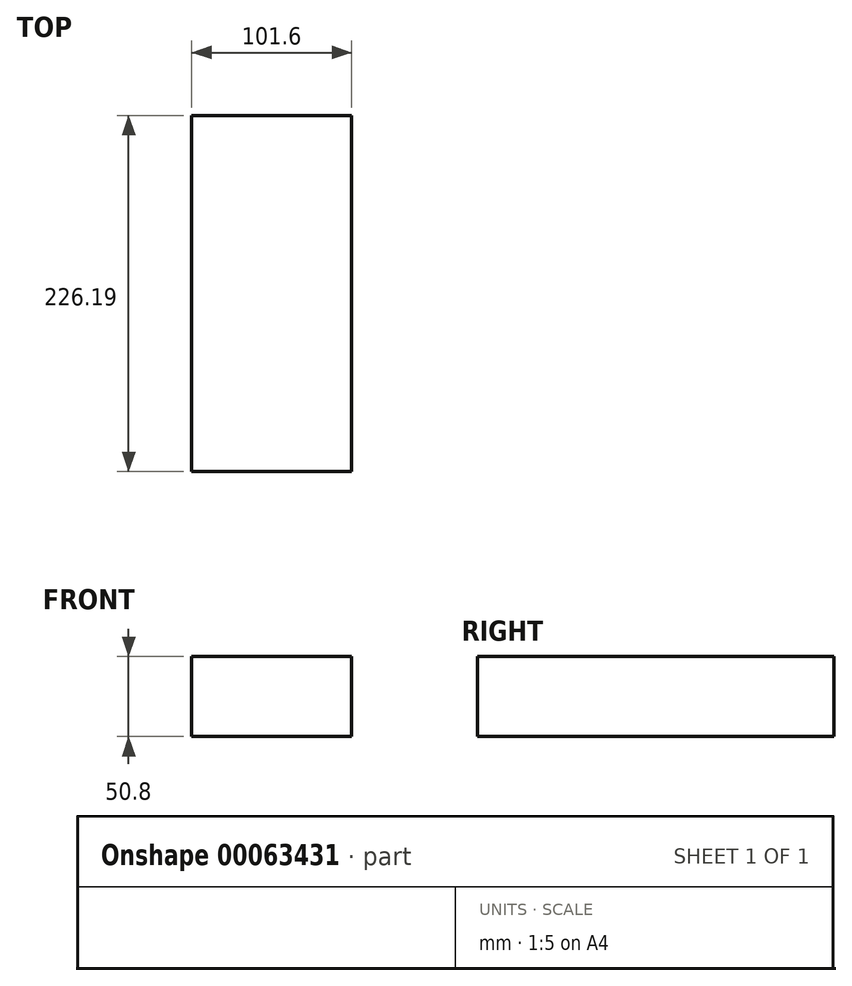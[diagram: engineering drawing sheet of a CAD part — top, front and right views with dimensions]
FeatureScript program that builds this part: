
annotation { "Feature Type Name" : "Feature", "Feature Type Description" : "" }
export const myFeature = defineFeature(function(context is Context, id is Id, definition is map)
    precondition{}
    {
        {
            var Q0;
            Q0=qCreatedBy(makeId("Front.planeOp"),FACE);
            var sketch = newSketch(context, id + "F0", { "sketchPlane" : qUnion([Q0])});
            skLineSegment(sketch, "E0.bottom", {"start": v(-50.8, 25.4) * mm, "end": v(50.8, 25.4) * mm});
            skLineSegment(sketch, "E0.top", {"start": v(-50.8, -25.4) * mm, "end": v(50.8, -25.4) * mm});
            skLineSegment(sketch, "E0.left", {"start": v(-50.8, 25.4) * mm, "end": v(-50.8, -25.4) * mm});
            skLineSegment(sketch, "E0.right", {"start": v(50.8, 25.4) * mm, "end": v(50.8, -25.4) * mm});
            skLineSegment(sketch, "E1", {"start": v(0, 61) * mm, "end": v(0, -65.86) * mm, "construction": true});
            skLineSegment(sketch, "E2", {"start": v(69.05, 0) * mm, "end": v(-62.97, 0) * mm, "construction": true});
            skSolve(sketch);
        }
        {
            var Q0;
            Q0 = qSketchRegion(id + "F0", true);
            extrude(context, id + "F1", {"entities" : qUnion([Q0]), "depth" : 200.8 * mm, "hasSecondDirection" : true, "secondDirectionOppositeDirection" : true, "secondDirectionDepth" : 25.4 * mm});
        }
    });
